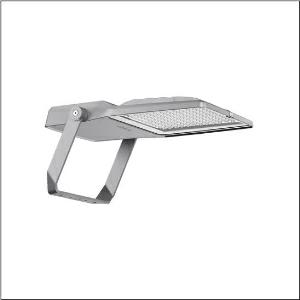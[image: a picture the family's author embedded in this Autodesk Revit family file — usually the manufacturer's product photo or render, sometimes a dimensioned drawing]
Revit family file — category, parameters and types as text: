
# Revit family: floodlight_fl_21_iq_midi___rs07_5xa7782f1b1a_00ed
name_source: partatom
category: Lighting Fixtures
units: mm (PartAtom-declared; Revit-internal decimal feet)

## family parameters
Cut with Voids When Loaded = No
Host = Face
Light Source = No
Part Type = Normal
Room Calculation Point = No
Round Connector Dimension = Use Diameter
Shared = No

## types (1)
- --- (1 x LED, 29450 lm, 270.2 W, 2200K)
    Apparent Load = 270 VA
    CIE Flux Codes = 79 92 99 100 100
    Color Rendering = 70
    Color Temperature = 2200K
    Default Elevation = 1800 mm
    Description = Floodlight FL 21 iQ midi, floodlight, primary light control with lens, of PMMA, primary optical cover: protective disc, of toughened safety glass, transparent, light distribution: RS07, light emission: direct distribution, installation type: surface-mounted, LED, High Power LED, rated luminous flux: 29.450lm, luminous efficacy: 109lm/W, light colour: 722, colour temperature: 2200K, control gear: ECG iQ, control: optimised constant luminous flux control (CLO 2.0), Desk-Remote (wireless, voltage-free reading and setting of iQ features in the workshop via application-optimized NFC function/RFID function), Smart-Wire, Night-Set, Temp-Guard, Street-Remote, Auto-Match, with terminal, 6-pole, mains connection: 220..240V, AC, 50/60Hz, start of lifetime: 270W, end of service life: 287W, reduction: 117W, luminaire housing, of diecast aluminium, powder-coated, Siteco® metallic grey (DB 702S), corrosivity category C5 mid according to DIN EN ISO 12944, sealing non-destructively replaceable, mounting bracket, of steel, galvanised, powder-coated, Siteco® metallic grey (DB 702S), protection rating (complete): IP66, insulation class (complete): insulation class II (safety insulation), certification: CE, protection symbol: D, impact resistance: IK08, permissible operating ambient temperature: -40..+40°C, permissible operating ambient temperature for outdoor applications: -40..+50°C, standard: DIN EN 12944, LABS conformity tested according to VDMA 24364:2018-05, packaging unit: 1 piece

Light Distribution: RS07
    Height = 76 mm
    Lamp = 1 x LED
    Lamp Light Flux = 29450 lm
    Lamp Power = 270.2 W
    Lamp count = 1
    Length = 657 mm
    Luminous efficacy = 109 lm/W
    Manufacturer = Siteco
    ModVariant = No
    Model = 5XA7782F1B1A
    Number of Poles = 1
    OnlyDefault = Yes
    Power Factor = 1
    Product Name = Floodlight FL 21 iQ midi | RS07
    Product group = floodlight | pylon annexe
    ProductGroupID = 6200
    Protection Class = Protection class II
    Protection Degree = IP 66
    RLX_Detail_Level = 1
    RLX_Emergency_Light_Flux = 0 lm
    RLX_Emergency_Type = 0
    RLX_Emergency_Type_DB = No
    RlxData = <blob elided: 141365 chars, md5=00388687>
    Socket = socket
    Standby Power = 0 W
    System Light Flux = 29450 lm
    System Power = 270 W
    Type Comments = factory setting: luminous flux: 100 % | dim-lin: 254 | 620 mA
    Type Image = l_1006876.jpg
    URL = http://relux.com
    VarID = @adj_055837
    Voltage = 0 V
    Weight = 0.00 kg
    Width = 442 mm

## geometry (parser evidence)
native form markers: Blend x4, Sweep x14
no freeform markers — native parametric forms only
